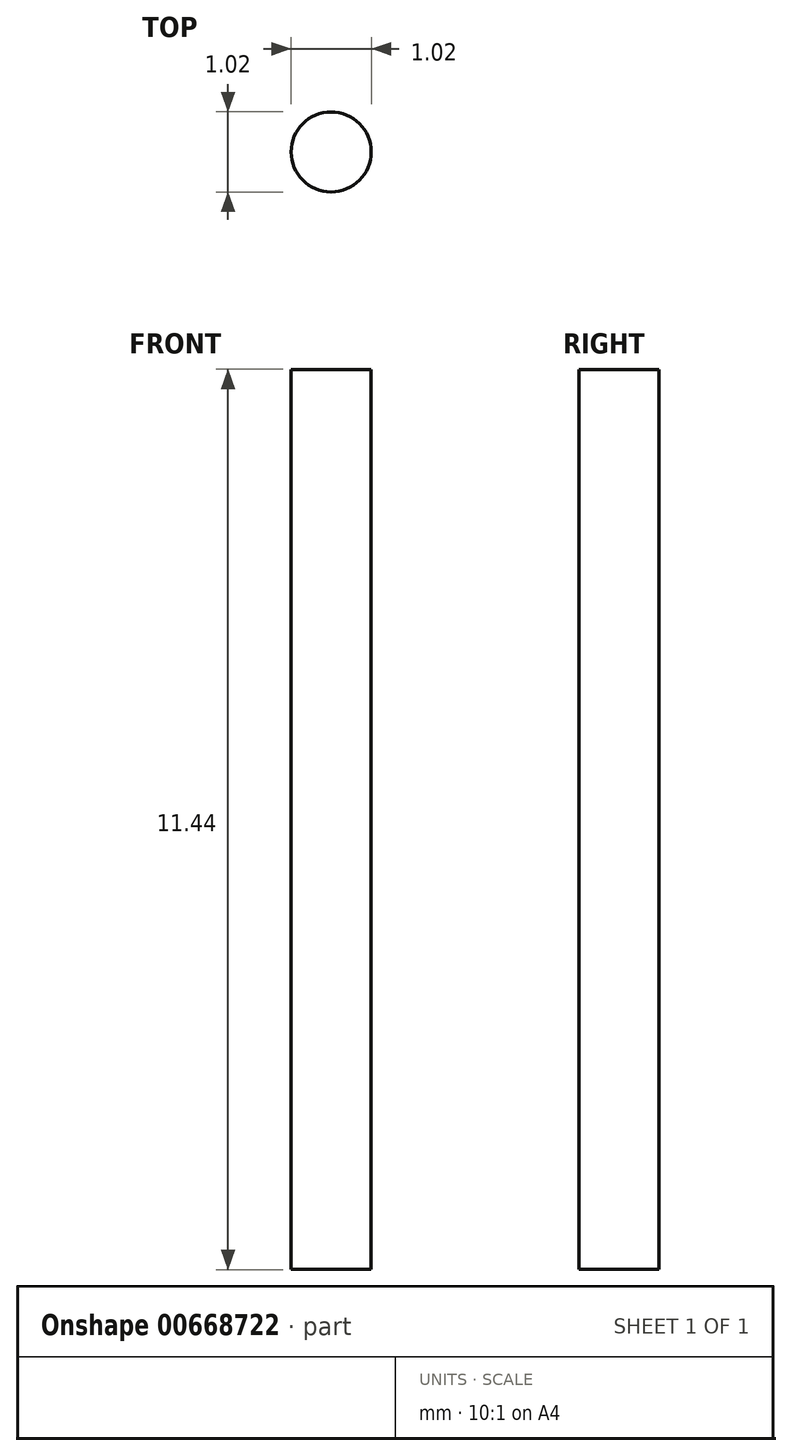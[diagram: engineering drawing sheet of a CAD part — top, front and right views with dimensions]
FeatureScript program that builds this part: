
annotation { "Feature Type Name" : "Feature", "Feature Type Description" : "" }
export const myFeature = defineFeature(function(context is Context, id is Id, definition is map)
    precondition{}
    {
        {
            var Q0;
            Q0=qCreatedBy(makeId("Top.planeOp"),FACE);
            var sketch = newSketch(context, id + "F0", { "sketchPlane" : qUnion([Q0])});
            skCircle(sketch, "E0", {"center": v(0, 0) * mm, "radius": 0.5 * mm});
            skSolve(sketch);
        }
        {
            var Q0;
            Q0 = qSketchRegion(id + "F0", true);
            extrude(context, id + "F1", {"entities" : qUnion([Q0]), "endBound" : BoundingType.SYMMETRIC, "depth" : 11.43 * mm, "offsetDistance" : 25.4 * mm});
        }
    });
